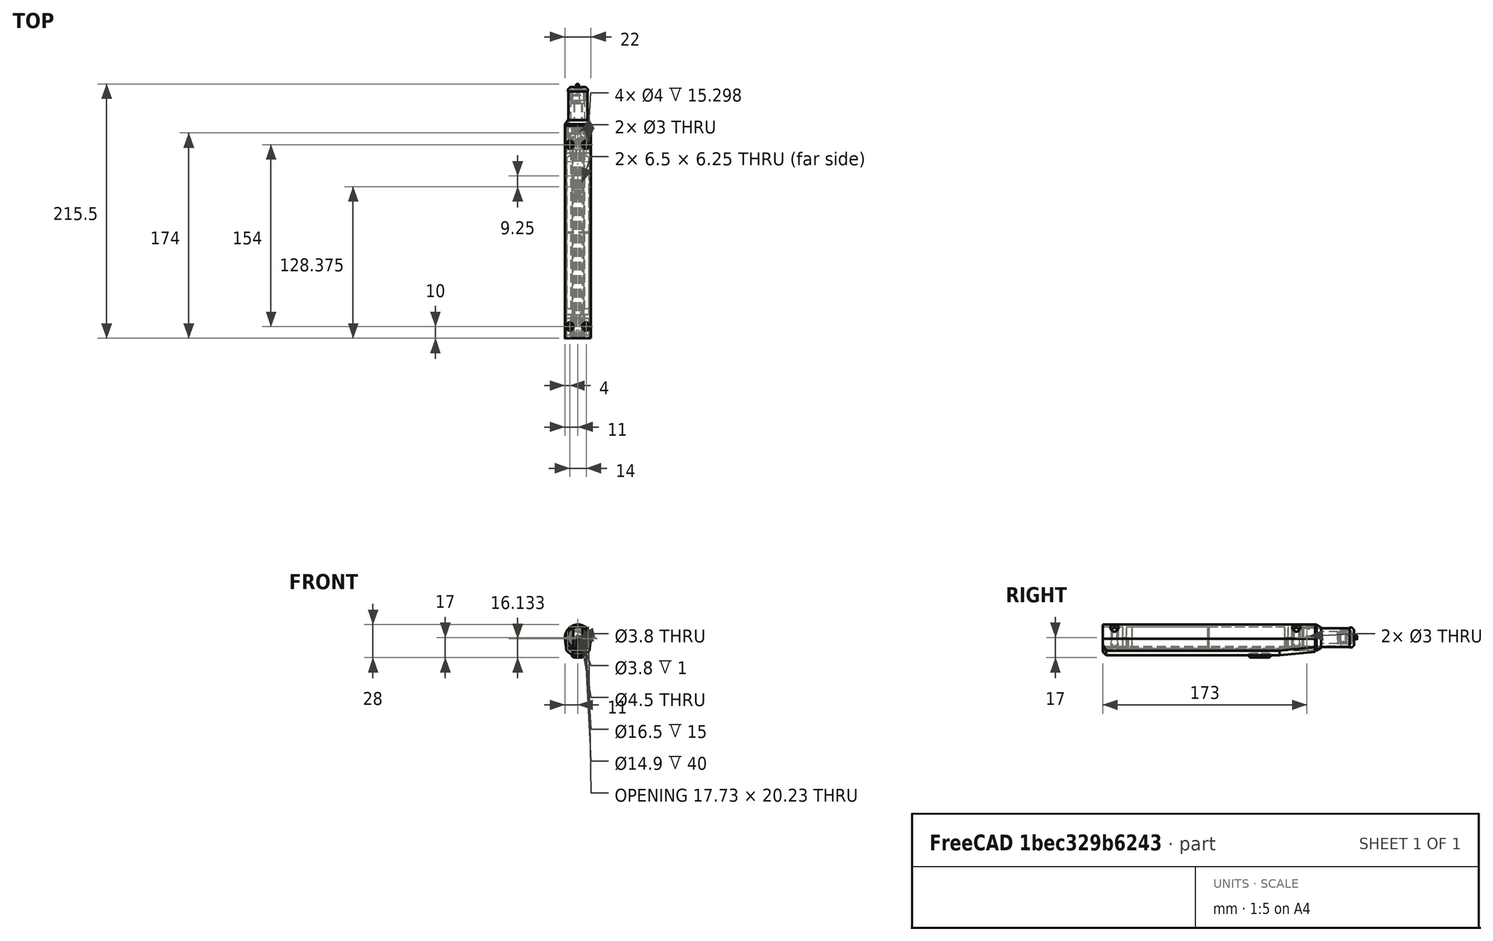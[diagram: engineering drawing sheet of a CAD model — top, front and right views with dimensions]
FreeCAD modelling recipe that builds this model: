
FCSTD DOCUMENT  (FreeCAD 0.20R29177 (Git))
Label: ScrewDriverV5
License: All rights reserved
LicenseURL: http://en.wikipedia.org/wiki/All_rights_reserved
objects: Sketcher::SketchObject×36, PartDesign::Pad×22, PartDesign::Pocket×12, PartDesign::Chamfer×10, PartDesign::Body×8, PartDesign::Fillet×7, PartDesign::Hole×1, PartDesign::Plane×1, PartDesign::LinearPattern×1
note: 150 computed .brp shape members not serialized (recipe doc carries the construction recipe); baked Part::Feature solids carry a one-line shape summary decoded from their .brp

FEATURE [Sketcher::SketchObject] Sketch001
  AttachmentOffset = pos=(0,0,30) rot=(0,0,1;0rad)
  FullyConstrained = true
  MapMode = 5
  Placement = pos=(0,-30,-6.7e-15) rot=(1,0,0;1.5708rad)
  Support = -> [XZ_Plane001]
  sketch-geometry (1):
    g0: Circle CenterX=0 CenterY=15 CenterZ=0 NormalX=0 NormalY=0 NormalZ=1 AngleXU=0 Radius=9
  constraints (3):
    c: PointOnObject(g0,g-2)
    c: Diameter(g0) = 18
    c: DistanceY(g-1,g0) = 15
FEATURE [PartDesign::Pad] Pad001  label="SingleBattery"
  Direction = (0,-1,2e-16)
  Length = 65
  Length2 = 10
  Placement = pos=(0,0,0) rot=(1,0,0;1.5708rad)
  Profile = -> Sketch001
  ReferenceAxis = -> Sketch001 [N_Axis]
  Type = 0
FEATURE [PartDesign::Fillet] Fillet001  label="BatteryFillet"
  Base = -> Pad001 [Edge2,Edge3]
  BaseFeature = -> Pad001
  Placement = pos=(0,0,0) rot=(1,0,0;1.5708rad)
  Radius = 1
  SupportTransform = false
  UseAllEdges = false
FEATURE [PartDesign::Body] Body001  label="18650I"
  Group = -> [Sketch001,Pad001,Fillet001]
  Origin = -> Origin001
  Placement = pos=(0,4,0) rot=(0,0,1;0rad)
  Tip = -> Fillet001
FEATURE [Sketcher::SketchObject] Sketch002
  AttachmentOffset = pos=(0,0,95) rot=(0,0,1;0rad)
  FullyConstrained = true
  MapMode = 5
  Placement = pos=(0,-95,-2.11e-14) rot=(1,0,0;1.5708rad)
  Support = -> [XZ_Plane002]
  sketch-geometry (1):
    g0: Circle CenterX=0 CenterY=15 CenterZ=0 NormalX=0 NormalY=0 NormalZ=1 AngleXU=0 Radius=9
  constraints (3):
    c: PointOnObject(g0,g-2)
    c: Diameter(g0) = 18
    c: DistanceY(g-1,g0) = 15
FEATURE [PartDesign::Pad] Pad002  label="SingleBattery001"
  Direction = (0,-1,-2e-16)
  Length = 65
  Length2 = 10
  Placement = pos=(0,0,0) rot=(1,0,0;1.5708rad)
  Profile = -> Sketch002
  ReferenceAxis = -> Sketch002 [N_Axis]
  Type = 0
FEATURE [PartDesign::Fillet] Fillet002  label="BatteryFillet001"
  Base = -> Pad002 [Edge2,Edge3]
  BaseFeature = -> Pad002
  Placement = pos=(0,0,0) rot=(1,0,0;1.5708rad)
  Radius = 1
  SupportTransform = false
  UseAllEdges = false
FEATURE [PartDesign::Body] Body002  label="18650II"
  Group = -> [Sketch002,Pad002,Fillet002]
  Origin = -> Origin002
  Placement = pos=(0,5,0) rot=(0,0,1;0rad)
  Tip = -> Fillet002
FEATURE [Sketcher::SketchObject] Sketch013
  AttachmentOffset = pos=(0,0,-10) rot=(0,0,1;0rad)
  FullyConstrained = true
  MapMode = 5
  Placement = pos=(0,10,2.2e-15) rot=(1,0,0;1.5708rad)
  Support = -> [XZ_Plane006]
  sketch-geometry (2):
    g0: Circle CenterX=0 CenterY=15 CenterZ=0 NormalX=0 NormalY=0 NormalZ=1 AngleXU=0 Radius=8.25
    g1: Circle CenterX=0 CenterY=15 CenterZ=0 NormalX=0 NormalY=0 NormalZ=1 AngleXU=0 Radius=11
  constraints (5):
    c: PointOnObject(g0,g-2)
    c: DistanceY(g-1,g0) = 15
    c: Diameter(g0) = 16.5
    c: Coincident(g1,g0)
    c: Diameter(g1) = 22
FEATURE [PartDesign::Pad] Pad007
  Direction = (0,-1,-2e-16)
  Length = 15
  Length2 = 10
  Placement = pos=(0,0,0) rot=(1,0,0;1.5708rad)
  Profile = -> Sketch013
  ReferenceAxis = -> Sketch013 [N_Axis]
  Type = 0
FEATURE [Sketcher::SketchObject] Sketch014
  AttachmentOffset = pos=(0,0,7) rot=(0,0,1;0rad)
  FullyConstrained = false
  MapMode = 5
  Placement = pos=(0,-7,-1.6e-15) rot=(1,0,0;1.5708rad)
  Support = -> [XZ_Plane006]
  sketch-geometry (2):
    g0: Circle CenterX=0.134772 CenterY=15 CenterZ=0 NormalX=0 NormalY=0 NormalZ=1 AngleXU=0 Radius=9.25
    g1: Circle CenterX=0.134772 CenterY=15 CenterZ=0 NormalX=0 NormalY=0 NormalZ=1 AngleXU=0 Radius=11.25
  constraints (4):
    c: Diameter(g0) = 18.5
    c: Coincident(g1,g0)
    c: Diameter(g1) = 22.5
    c: DistanceY(g-1,g0) = 15
FEATURE [PartDesign::Pocket] Pocket006
  BaseFeature = -> Pad007
  Direction = (0,1,2e-16)
  Length = 12
  Length2 = 1
  Placement = pos=(0,0,0) rot=(1,0,0;1.5708rad)
  Profile = -> Sketch014
  ReferenceAxis = -> Sketch014 [N_Axis]
  Type = 0
FEATURE [PartDesign::Chamfer] Chamfer006
  Angle = 45
  Base = -> Pocket006 [Edge1]
  BaseFeature = -> Pocket006
  ChamferType = 1
  FlipDirection = false
  Placement = pos=(0,0,0) rot=(1,0,0;1.5708rad)
  Size = 4
  Size2 = 1.5
  SupportTransform = false
  UseAllEdges = false
FEATURE [Sketcher::SketchObject] Sketch015
  AttachmentOffset = pos=(0,4,5) rot=(0,0,1;0rad)
  FullyConstrained = false
  MapMode = 5
  Placement = pos=(0,4,5) rot=(0,0,1;0rad)
  Support = -> [XY_Plane006]
  sketch-geometry (1):
    g0: Circle CenterX=0.028156 CenterY=-7.03327 CenterZ=0 NormalX=0 NormalY=0 NormalZ=1 AngleXU=0 Radius=1.5
  constraints (1):
    c: Diameter(g0) = 3
FEATURE [PartDesign::Hole] Hole
  BaseFeature = -> Chamfer006
  CustomThreadClearance = 0
  Depth = 25
  DepthType = 0
  Diameter = 2.5
  DrillForDepth = false
  DrillPoint = 1
  DrillPointAngle = 118
  HoleCutCountersinkAngle = 90
  HoleCutCustomValues = false
  HoleCutDepth = 0
  HoleCutDiameter = 6.1
  HoleCutType = 0
  ModelThread = false
  Placement = pos=(0,0,0) rot=(1,0,0;1.5708rad)
  Profile = -> Sketch015
  Tapered = false
  TaperedAngle = 90
  ThreadClass = 0
  ThreadDepth = 25
  ThreadDepthType = 0
  ThreadDirection = 0
  ThreadFit = 0
  ThreadSize = 9
  ThreadType = 1
  Threaded = true
  UseCustomThreadClearance = false
FEATURE [PartDesign::Plane] DatumPlane
  Length = 61.4018
  Placement = pos=(0,0,15) rot=(0,0,1;0rad)
  ResizeMode = 0
  Width = 76.4018
FEATURE [Sketcher::SketchObject] Sketch003
  FullyConstrained = true
  MapMode = 5
  Placement = pos=(0,0,0) rot=(1,0,0;1.5708rad)
  Support = -> [XZ_Plane003]
  sketch-geometry (1):
    g0: Circle CenterX=0 CenterY=15 CenterZ=0 NormalX=0 NormalY=0 NormalZ=1 AngleXU=0 Radius=8
  constraints (3):
    c: PointOnObject(g0,g-2)
    c: Diameter(g0) = 16
    c: DistanceY(g-1,g0) = 15
FEATURE [PartDesign::Pad] Pad003
  Direction = (0,-1,-2e-16)
  Length = 40
  Length2 = 10
  Placement = pos=(0,0,0) rot=(1,0,0;1.5708rad)
  Profile = -> Sketch003
  ReferenceAxis = -> Sketch003 [N_Axis]
  Reversed = true
  Type = 0
FEATURE [Sketcher::SketchObject] Sketch004
  FullyConstrained = true
  MapMode = 5
  Placement = pos=(0,0,15) rot=(0,0,1;0rad)
  Support = -> [DatumPlane]
  sketch-geometry (1):
    g0: Circle CenterX=0 CenterY=5 CenterZ=0 NormalX=0 NormalY=0 NormalZ=1 AngleXU=0 Radius=1.5
  constraints (3):
    c: PointOnObject(g0,g-2)
    c: Diameter(g0) = 3
    c: DistanceY(g-1,g0) = 5
FEATURE [PartDesign::Pocket] Pocket
  BaseFeature = -> Pad003
  Direction = (0,0,-1)
  Length = 27
  Length2 = 5
  Midplane = true
  Placement = pos=(0,0,0) rot=(1,0,0;1.5708rad)
  Profile = -> Sketch004
  ReferenceAxis = -> Sketch004 [N_Axis]
  Type = 0
FEATURE [Sketcher::SketchObject] Sketch005
  ExternalGeometry = -> [Pocket]
  FullyConstrained = true
  MapMode = 5
  Placement = pos=(0,0,0) rot=(1,0,0;1.5708rad)
  Support = -> [XZ_Plane003]
  sketch-geometry (1):
    g0: Circle CenterX=0 CenterY=15 CenterZ=0 NormalX=0 NormalY=0 NormalZ=1 AngleXU=0 Radius=7.45
  constraints (3):
    c: Coincident(g0,g-3)
    c: Diameter(g-3) = 16
    c: Diameter(g0) = 14.9
FEATURE [PartDesign::Pocket] Pocket001
  BaseFeature = -> Pocket
  Direction = (0,1,2e-16)
  Length = 5
  Length2 = 5
  Placement = pos=(0,0,0) rot=(1,0,0;1.5708rad)
  Profile = -> Sketch005
  ReferenceAxis = -> Sketch005 [N_Axis]
  Type = 1
FEATURE [Sketcher::SketchObject] Sketch016
  FullyConstrained = false
  MapMode = 5
  Support = -> [XY_Plane003]
  sketch-geometry (1):
    g0: Circle CenterX=0 CenterY=4.973 CenterZ=0 NormalX=0 NormalY=0 NormalZ=1 AngleXU=0 Radius=1.25
  constraints (2):
    c: PointOnObject(g0,g-2)
    c: Diameter(g0) = 2.5
FEATURE [PartDesign::Body] Body003  label="MetalPipe"
  Group = -> [Sketch003,Pad003,DatumPlane,Sketch004,Pocket,Sketch005,Pocket001,Sketch016]
  Origin = -> Origin003
  Placement = pos=(0,-11,0) rot=(0,0,1;0rad)
  Tip = -> Pocket001
FEATURE [PartDesign::Chamfer] Chamfer008
  Angle = 45
  Base = -> Hole [Edge5]
  BaseFeature = -> Hole
  ChamferType = 1
  FlipDirection = false
  Placement = pos=(0,0,0) rot=(1,0,0;1.5708rad)
  Size = 4
  Size2 = 1
  SupportTransform = false
  UseAllEdges = false
FEATURE [Sketcher::SketchObject] Sketch022
  FullyConstrained = true
  MapMode = 5
  Placement = pos=(0,0,0) rot=(1,0,0;1.5708rad)
  Support = -> [XZ_Plane007]
  sketch-geometry (4):
    g0: LineSegment StartX=-3.5 StartY=19.8734 StartZ=0 EndX=3.5 EndY=19.8734 EndZ=0
    g1: LineSegment StartX=3.11736 StartY=9.8734 StartZ=0 EndX=-3.11736 EndY=9.8734 EndZ=0
    g2: ArcOfCircle CenterX=0 CenterY=15 CenterZ=0 NormalX=0 NormalY=0 NormalZ=1 AngleXU=0 Radius=6 StartAngle=2.19362 EndAngle=4.16605
    g3: ArcOfCircle CenterX=0 CenterY=15 CenterZ=0 NormalX=0 NormalY=0 NormalZ=1 AngleXU=0 Radius=6 StartAngle=5.25873 EndAngle=7.23116
  constraints (13):
    c: Horizontal(g0)
    c: Horizontal(g1)
    c: PointOnObject(g2,g-2)
    c: DistanceY(g-1,g2) = 15
    c: Coincident(g3,g0)
    c: Coincident(g2,g0)
    c: Equal(g2,g3)
    c: Coincident(g2,g1)
    c: Coincident(g2,g3)
    c: DistanceX(g0,g0) = 7
    c: DistanceY(g1,g0) = 10
    c: Coincident(g3,g1)
    c: Radius(g2) = 6
FEATURE [PartDesign::Pad] Pad011
  Direction = (0,-1,2e-16)
  Length = 14.6
  Length2 = 10
  Placement = pos=(0,0,0) rot=(1,0,0;1.5708rad)
  Profile = -> Sketch022
  ReferenceAxis = -> Sketch022 [N_Axis]
  Type = 0
FEATURE [Sketcher::SketchObject] Sketch023
  ExternalGeometry = -> [Pad011]
  FullyConstrained = true
  MapMode = 5
  Placement = pos=(0,0,0) rot=(-1,0,0;1.5708rad)
  Support = -> [Pad011]
  sketch-geometry (4):
    g0: LineSegment StartX=-6 StartY=-10 StartZ=0 EndX=6 EndY=-10 EndZ=0
    g1: LineSegment StartX=6 StartY=-10 StartZ=0 EndX=6 EndY=-20 EndZ=0
    g2: LineSegment StartX=6 StartY=-20 StartZ=0 EndX=-6 EndY=-20 EndZ=0
    g3: LineSegment StartX=-6 StartY=-20 StartZ=0 EndX=-6 EndY=-10 EndZ=0
  constraints (12):
    c: Coincident(g0,g1)
    c: Coincident(g1,g2)
    c: Coincident(g2,g3)
    c: Coincident(g3,g0)
    c: Horizontal(g0)
    c: Horizontal(g2)
    c: Vertical(g1)
    c: Vertical(g3)
    c: DistanceX(g0,g0) = 12
    c: DistanceX(g-3,g0) = 6
    c: DistanceY(g-3,g0) = 5
    c: DistanceY(g1,g-3) = 5
FEATURE [PartDesign::Pad] Pad012
  BaseFeature = -> Pad011
  Direction = (0,1,-2e-16)
  Length = 1
  Length2 = 10
  Placement = pos=(0,0,0) rot=(1,0,0;1.5708rad)
  Profile = -> Sketch023
  ReferenceAxis = -> Sketch023 [N_Axis]
  Type = 0
FEATURE [PartDesign::Fillet] Fillet003
  Base = -> Pad012 [Edge28,Edge26,Edge25,Edge30]
  BaseFeature = -> Pad012
  Placement = pos=(0,0,0) rot=(1,0,0;1.5708rad)
  Radius = 0.5
  SupportTransform = false
  UseAllEdges = false
FEATURE [Sketcher::SketchObject] Sketch024
  FullyConstrained = false
  MapMode = 5
  Placement = pos=(0,0,0) rot=(1,0,0;1.5708rad)
  Support = -> [XZ_Plane007]
  sketch-geometry (4):
    g0: Circle CenterX=-5.3769 CenterY=19.2954 CenterZ=0 NormalX=0 NormalY=0 NormalZ=1 AngleXU=0 Radius=0.455689
    g1: Circle CenterX=-5.39544 CenterY=10.6161 CenterZ=0 NormalX=0 NormalY=0 NormalZ=1 AngleXU=0 Radius=0.455689
    g2: Circle CenterX=5.39544 CenterY=10.6161 CenterZ=0 NormalX=0 NormalY=0 NormalZ=1 AngleXU=0 Radius=0.455689
    g3: Circle CenterX=5.3769 CenterY=19.2954 CenterZ=0 NormalX=0 NormalY=0 NormalZ=1 AngleXU=0 Radius=0.455689
  constraints (5):
    c: Equal(g3,g2)
    c: Equal(g2,g1)
    c: Equal(g1,g0)
    c: Symmetric(g3,g0,g-2)
    c: Symmetric(g2,g1,g-2)
FEATURE [PartDesign::Pad] Pad013
  BaseFeature = -> Fillet003
  Direction = (0,-1,2e-16)
  Length = 7.5
  Length2 = 10
  Placement = pos=(0,0,0) rot=(1,0,0;1.5708rad)
  Profile = -> Sketch024
  ReferenceAxis = -> Sketch024 [N_Axis]
  Reversed = true
  Type = 0
FEATURE [Sketcher::SketchObject] Sketch025
  AttachmentOffset = pos=(0,0,-7.5) rot=(0,0,1;0rad)
  ExternalGeometry = -> [Pad013]
  FullyConstrained = true
  MapMode = 5
  Placement = pos=(0,7.5,1.7e-15) rot=(1,0,0;1.5708rad)
  Support = -> [XZ_Plane007]
  sketch-geometry (4):
    g0: LineSegment StartX=-6 StartY=20 StartZ=0 EndX=6 EndY=20 EndZ=0
    g1: LineSegment StartX=6 StartY=20 StartZ=0 EndX=6 EndY=10 EndZ=0
    g2: LineSegment StartX=6 StartY=10 StartZ=0 EndX=-6 EndY=10 EndZ=0
    g3: LineSegment StartX=-6 StartY=10 StartZ=0 EndX=-6 EndY=20 EndZ=0
  constraints (12):
    c: Coincident(g0,g1)
    c: Coincident(g1,g2)
    c: Coincident(g2,g3)
    c: Coincident(g3,g0)
    c: Horizontal(g0)
    c: Horizontal(g2)
    c: Vertical(g1)
    c: Vertical(g3)
    c: DistanceX(g0,g0) = 12
    c: DistanceX(g0,g-3) = 6
    c: DistanceY(g1,g1) = 10
    c: DistanceY(g-3,g0) = 5
FEATURE [PartDesign::Pad] Pad014
  BaseFeature = -> Pad013
  Direction = (0,-1,2e-16)
  Length = 1
  Length2 = 10
  Placement = pos=(0,0,0) rot=(1,0,0;1.5708rad)
  Profile = -> Sketch025
  ReferenceAxis = -> Sketch025 [N_Axis]
  Type = 0
FEATURE [Sketcher::SketchObject] Sketch026
  ExternalGeometry = -> [Pad014]
  FullyConstrained = true
  MapMode = 5
  Placement = pos=(0,7.5,-3e-15) rot=(-1,0,0;1.5708rad)
  Support = -> [Pad014]
  sketch-geometry (1):
    g0: Circle CenterX=0 CenterY=-15 CenterZ=0 NormalX=0 NormalY=0 NormalZ=1 AngleXU=0 Radius=1.9
  constraints (2):
    c: Coincident(g0,g-3)
    c: Diameter(g0) = 3.8
FEATURE [PartDesign::Pocket] Pocket008
  BaseFeature = -> Pad014
  Direction = (0,-1,2e-16)
  Length = 7.5
  Length2 = 5
  Placement = pos=(0,0,0) rot=(1,0,0;1.5708rad)
  Profile = -> Sketch026
  ReferenceAxis = -> Sketch026 [N_Axis]
  Type = 0
FEATURE [Sketcher::SketchObject] Sketch027
  ExternalGeometry = -> [Pocket008]
  FullyConstrained = true
  MapMode = 5
  Placement = pos=(0,7.5,-3e-15) rot=(-1,0,0;1.5708rad)
  Support = -> [Pocket008]
  sketch-geometry (1):
    g0: Circle CenterX=0 CenterY=-15 CenterZ=0 NormalX=0 NormalY=0 NormalZ=1 AngleXU=0 Radius=1.45
  constraints (2):
    c: Coincident(g0,g-3)
    c: Diameter(g0) = 2.9
FEATURE [PartDesign::Pad] Pad015
  BaseFeature = -> Pocket008
  Direction = (0,1,-2e-16)
  Length = 18
  Length2 = 10
  Midplane = true
  Placement = pos=(0,0,0) rot=(1,0,0;1.5708rad)
  Profile = -> Sketch027
  ReferenceAxis = -> Sketch027 [N_Axis]
  Type = 0
FEATURE [PartDesign::Fillet] Fillet004
  Base = -> Pad015 [Edge70,Edge73,Edge75,Edge71]
  BaseFeature = -> Pad015
  Placement = pos=(0,0,0) rot=(1,0,0;1.5708rad)
  Radius = 0.5
  SupportTransform = false
  UseAllEdges = false
FEATURE [Sketcher::SketchObject] Sketch028
  AttachmentOffset = pos=(0,0,-7) rot=(0,0,1;0rad)
  ExternalGeometry = -> [Fillet004]
  FullyConstrained = true
  MapMode = 5
  Placement = pos=(0,7,1.6e-15) rot=(1,0,0;1.5708rad)
  Support = -> [XZ_Plane007]
  sketch-geometry (2):
    g0: ArcOfCircle CenterX=0 CenterY=15 CenterZ=0 NormalX=0 NormalY=0 NormalZ=1 AngleXU=0 Radius=1.45 StartAngle=5.38201 EndAngle=7.18436
    g1: LineSegment StartX=0.9 StartY=13.8631 StartZ=0 EndX=0.9 EndY=16.1369 EndZ=0
  constraints (6):
    c: Coincident(g0,g-3)
    c: PointOnObject(g0,g-3)
    c: DistanceX(g0,g0) = 0.9
    c: DistanceX(g0,g0) = 0.9
    c: Coincident(g1,g0)
    c: Coincident(g1,g0)
FEATURE [PartDesign::Pocket] Pocket009
  BaseFeature = -> Fillet004
  Direction = (0,1,-2e-16)
  Length = 10
  Length2 = 5
  Placement = pos=(0,0,0) rot=(1,0,0;1.5708rad)
  Profile = -> Sketch028
  ReferenceAxis = -> Sketch028 [N_Axis]
  Type = 0
FEATURE [PartDesign::Body] Body007  label="Engine"
  Group = -> [Sketch022,Pad011,Sketch023,Pad012,Fillet003,Sketch024,Pad013,Sketch025,Pad014,Sketch026,Pocket008,Sketch027,Pad015,Fillet004,Sketch028,Pocket009]
  Origin = -> Origin007
  Placement = pos=(0,19,0) rot=(0,0,1;0rad)
  Tip = -> Pocket009
FEATURE [Sketcher::SketchObject] Sketch029
  FullyConstrained = true
  MapMode = 5
  Placement = pos=(0,0,0) rot=(1,0,0;1.5708rad)
  Support = -> [XZ_Plane008]
  sketch-geometry (2):
    g0: Circle CenterX=0 CenterY=15 CenterZ=0 NormalX=0 NormalY=0 NormalZ=1 AngleXU=0 Radius=2.25
    g1: Circle CenterX=0 CenterY=15 CenterZ=0 NormalX=0 NormalY=0 NormalZ=1 AngleXU=0 Radius=7.35
  constraints (5):
    c: PointOnObject(g0,g-2)
    c: Coincident(g1,g0)
    c: DistanceY(g-1,g0) = 15
    c: Diameter(g0) = 4.5
    c: Diameter(g1) = 14.7
FEATURE [PartDesign::Pad] Pad016
  Direction = (0,-1,2e-16)
  Length = 2.5
  Length2 = 10
  Placement = pos=(0,0,0) rot=(1,0,0;1.5708rad)
  Profile = -> Sketch029
  ReferenceAxis = -> Sketch029 [N_Axis]
  Reversed = true
  Type = 0
FEATURE [Sketcher::SketchObject] Sketch030
  ExternalGeometry = -> [Pad016]
  FullyConstrained = false
  MapMode = 5
  Placement = pos=(0,2.5,-1.1e-15) rot=(-1,0,0;1.5708rad)
  Support = -> [Pad016]
  sketch-geometry (8):
    g0: LineSegment StartX=-4.88664 StartY=-20.4903 StartZ=0 EndX=4.88664 EndY=-20.4903 EndZ=0
    g1: LineSegment StartX=6.43814 StartY=-18.5458 StartZ=0 EndX=6.43814 EndY=-11.4542 EndZ=0
    g2: LineSegment StartX=4.68852 StartY=-9.33959 StartZ=0 EndX=-4.68852 EndY=-9.33959 EndZ=0
    g3: LineSegment StartX=-6.45711 StartY=-11.4888 StartZ=0 EndX=-6.45711 EndY=-18.5112 EndZ=0
    g4: ArcOfCircle CenterX=0 CenterY=-15 CenterZ=0 NormalX=0 NormalY=0 NormalZ=1 AngleXU=0 Radius=7.35 StartAngle=2.64355 EndAngle=3.63964
    g5: ArcOfCircle CenterX=0 CenterY=-15 CenterZ=0 NormalX=0 NormalY=0 NormalZ=1 AngleXU=0 Radius=7.35 StartAngle=3.9851 EndAngle=5.43968
    g6: ArcOfCircle CenterX=0 CenterY=-15 CenterZ=0 NormalX=0 NormalY=0 NormalZ=1 AngleXU=0 Radius=7.35 StartAngle=5.77977 EndAngle=6.7866
    g7: ArcOfCircle CenterX=0 CenterY=-15 CenterZ=0 NormalX=0 NormalY=0 NormalZ=1 AngleXU=0 Radius=7.35 StartAngle=0.879035 EndAngle=2.26256
  constraints (26):
    c: PointOnObject(g0,g-3)
    c: PointOnObject(g0,g-3)
    c: Horizontal(g0)
    c: PointOnObject(g1,g-3)
    c: PointOnObject(g1,g-3)
    c: Vertical(g1)
    c: PointOnObject(g2,g-3)
    c: PointOnObject(g2,g-3)
    c: Horizontal(g2)
    c: PointOnObject(g3,g-3)
    c: Vertical(g3)
    c: Coincident(g4,g-3)
    c: Coincident(g7,g2)
    c: Coincident(g4,g3)
    c: Equal(g4,g5)
    c: PointOnObject(g4,g3)
    c: PointOnObject(g5,g0)
    c: Coincident(g4,g5)
    c: Equal(g5,g6)
    c: PointOnObject(g5,g0)
    c: PointOnObject(g6,g1)
    c: Coincident(g5,g6)
    c: Equal(g6,g7)
    c: PointOnObject(g6,g1)
    c: PointOnObject(g7,g2)
    c: Coincident(g6,g7)
FEATURE [PartDesign::Pad] Pad017
  BaseFeature = -> Pad016
  Direction = (0,1,-2e-16)
  Length = 9
  Length2 = 10
  Placement = pos=(0,0,0) rot=(1,0,0;1.5708rad)
  Profile = -> Sketch030
  ReferenceAxis = -> Sketch030 [N_Axis]
  Type = 0
FEATURE [PartDesign::Chamfer] Chamfer010
  Angle = 45
  Base = -> Pad017 [Edge12]
  BaseFeature = -> Pad017
  ChamferType = 1
  FlipDirection = false
  Placement = pos=(0,0,0) rot=(1,0,0;1.5708rad)
  Size = 2
  Size2 = 2
  SupportTransform = false
  UseAllEdges = false
FEATURE [Sketcher::SketchObject] Sketch031
  ExternalGeometry = -> [Chamfer010]
  FullyConstrained = true
  MapMode = 5
  Placement = pos=(0,0,0) rot=(1,0,0;1.5708rad)
  Support = -> [Chamfer010]
  sketch-geometry (2):
    g0: Circle CenterX=0 CenterY=15 CenterZ=0 NormalX=0 NormalY=0 NormalZ=1 AngleXU=0 Radius=8.4
    g1: Circle CenterX=0 CenterY=15 CenterZ=0 NormalX=0 NormalY=0 NormalZ=1 AngleXU=0 Radius=7.35
  constraints (4):
    c: Coincident(g0,g-3)
    c: Diameter(g0) = 16.8
    c: Coincident(g1,g0)
    c: Diameter(g1) = 14.7
FEATURE [PartDesign::Pad] Pad018
  BaseFeature = -> Chamfer010
  Direction = (0,-1,4e-16)
  Length = 4
  Length2 = 10
  Placement = pos=(0,0,0) rot=(1,0,0;1.5708rad)
  Profile = -> Sketch031
  ReferenceAxis = -> Sketch031 [N_Axis]
  Reversed = true
  Type = 0
FEATURE [PartDesign::Chamfer] Chamfer011
  Angle = 45
  Base = -> Pad018 [Edge5]
  BaseFeature = -> Pad018
  ChamferType = 0
  FlipDirection = false
  Placement = pos=(0,0,0) rot=(1,0,0;1.5708rad)
  Size = 2
  Size2 = 1
  SupportTransform = false
  UseAllEdges = false
FEATURE [PartDesign::Fillet] Fillet005
  Base = -> Chamfer011 [Edge4]
  BaseFeature = -> Chamfer011
  Placement = pos=(0,0,0) rot=(1,0,0;1.5708rad)
  Radius = 1
  SupportTransform = false
  UseAllEdges = false
FEATURE [PartDesign::Body] Body008  label="EngineHolder"
  Group = -> [Sketch029,Pad016,Sketch030,Pad017,Chamfer010,Sketch031,Pad018,Chamfer011,Fillet005]
  Origin = -> Origin008
  Placement = pos=(0,33,30) rot=(1,0,0;3.14159rad)
  Tip = -> Fillet005
FEATURE [Sketcher::SketchObject] Sketch035
  FullyConstrained = true
  MapMode = 5
  Support = -> [XY_Plane009]
  sketch-geometry (4):
    g0: LineSegment StartX=-5.5 StartY=-37 StartZ=0 EndX=5.5 EndY=-37 EndZ=0
    g1: LineSegment StartX=5.5 StartY=-37 StartZ=0 EndX=5.5 EndY=-57 EndZ=0
    g2: LineSegment StartX=5.5 StartY=-57 StartZ=0 EndX=-5.5 EndY=-57 EndZ=0
    g3: LineSegment StartX=-5.5 StartY=-57 StartZ=0 EndX=-5.5 EndY=-37 EndZ=0
  constraints (12):
    c: Coincident(g0,g1)
    c: Coincident(g1,g2)
    c: Coincident(g2,g3)
    c: Coincident(g3,g0)
    c: Horizontal(g0)
    c: Horizontal(g2)
    c: Vertical(g1)
    c: Vertical(g3)
    c: DistanceY(g0,g-1) = 37
    c: DistanceX(g0,g-1) = 5.5
    c: DistanceX(g-1,g1) = 5.5
    c: DistanceY(g1,g1) = 20
FEATURE [PartDesign::Pad] Pad019
  Direction = (0,0,1)
  Length = 2
  Length2 = 10
  Profile = -> Sketch035
  ReferenceAxis = -> Sketch035 [N_Axis]
  Reversed = true
  Type = 0
FEATURE [Sketcher::SketchObject] Sketch036
  ExternalGeometry = -> [Pad019]
  FullyConstrained = true
  MapMode = 5
  Support = -> [XY_Plane009]
  sketch-geometry (8):
    g0: LineSegment StartX=-3.25 StartY=-39.25 StartZ=0 EndX=3.25 EndY=-39.25 EndZ=0
    g1: LineSegment StartX=3.25 StartY=-39.25 StartZ=0 EndX=3.25 EndY=-45.5 EndZ=0
    g2: LineSegment StartX=3.25 StartY=-54.75 StartZ=0 EndX=-3.25 EndY=-54.75 EndZ=0
    g3: LineSegment StartX=-3.25 StartY=-54.75 StartZ=0 EndX=-3.25 EndY=-48.5 EndZ=0
    g4: LineSegment StartX=-3.25 StartY=-45.5 StartZ=0 EndX=3.25 EndY=-45.5 EndZ=0
    g5: LineSegment StartX=3.25 StartY=-48.5 StartZ=0 EndX=-3.25 EndY=-48.5 EndZ=0
    g6: LineSegment StartX=3.25 StartY=-48.5 StartZ=0 EndX=3.25 EndY=-54.75 EndZ=0
    g7: LineSegment StartX=-3.25 StartY=-45.5 StartZ=0 EndX=-3.25 EndY=-39.25 EndZ=0
  constraints (24):
    c: Coincident(g0,g1)
    c: Coincident(g6,g2)
    c: Coincident(g2,g3)
    c: Coincident(g7,g0)
    c: Horizontal(g0)
    c: Horizontal(g2)
    c: Vertical(g1)
    c: Vertical(g3)
    c: DistanceX(g-5,g0) = 2.25
    c: Horizontal(g4)
    c: Horizontal(g5)
    c: DistanceY(g4,g0) = 6.25
    c: DistanceY(g6,g5) = 6.25
    c: Coincident(g7,g4)
    c: Vertical(g6)
    c: Coincident(g6,g5)
    c: DistanceX(g0,g0) = 6.5
    c: DistanceX(g5,g5) = 6.5
    c: Coincident(g5,g3)
    c: Coincident(g4,g1)
    c: Vertical(g7)
    c: DistanceY(g-5,g2) = 2.25
    c: DistanceX(g-5,g2) = 2.25
    c: DistanceY(g0,g-4) = 2.25
FEATURE [PartDesign::Pocket] Pocket012
  BaseFeature = -> Pad019
  Direction = (0,0,-1)
  Length = 5
  Length2 = 5
  Profile = -> Sketch036
  ReferenceAxis = -> Sketch036 [N_Axis]
  Type = 0
FEATURE [PartDesign::Fillet] Fillet007
  Base = -> Pocket012 [Edge1,Edge2,Edge8,Edge5]
  BaseFeature = -> Pocket012
  Radius = 2
  SupportTransform = false
  UseAllEdges = false
FEATURE [PartDesign::Chamfer] Chamfer
  Angle = 45
  Base = -> Fillet007 [Edge4,Edge21,Edge23,Edge25,Edge27,Edge28,Edge24,Edge26]
  BaseFeature = -> Fillet007
  ChamferType = 0
  FlipDirection = false
  Size = 1.9
  Size2 = 1
  SupportTransform = false
  UseAllEdges = false
FEATURE [Sketcher::SketchObject] Sketch037
  AttachmentOffset = pos=(0,0,36) rot=(0,0,1;0rad)
  ExternalGeometry = -> [Sketch035]
  FullyConstrained = false
  MapMode = 5
  Placement = pos=(0,-36,-8e-15) rot=(1,0,0;1.5708rad)
  Support = -> [XZ_Plane009]
  sketch-geometry (8):
    g0: LineSegment StartX=4.99997 StartY=0 StartZ=0 EndX=6.38463 EndY=0 EndZ=0
    g1: LineSegment StartX=6.38463 StartY=0 StartZ=0 EndX=6.38463 EndY=-1.93807 EndZ=0
    g2: LineSegment StartX=6.38463 StartY=-1.93807 StartZ=0 EndX=4.99997 EndY=-1.93807 EndZ=0
    g3: LineSegment StartX=4.99997 StartY=-1.93807 StartZ=0 EndX=4.99997 EndY=0 EndZ=0
    g4: LineSegment StartX=-5.00036 StartY=0 StartZ=0 EndX=-5.88621 EndY=0 EndZ=0
    g5: LineSegment StartX=-5.88621 StartY=0 StartZ=0 EndX=-5.88621 EndY=-2.0574 EndZ=0
    g6: LineSegment StartX=-5.88621 StartY=-2.0574 StartZ=0 EndX=-5.00036 EndY=-2.0574 EndZ=0
    g7: LineSegment StartX=-5.00036 StartY=-2.0574 StartZ=0 EndX=-5.00036 EndY=0 EndZ=0
  constraints (18):
    c: Coincident(g0,g1)
    c: Coincident(g1,g2)
    c: Coincident(g2,g3)
    c: Coincident(g3,g0)
    c: Horizontal(g0)
    c: Horizontal(g2)
    c: Vertical(g1)
    c: Vertical(g3)
    c: PointOnObject(g0,g-1)
    c: Coincident(g4,g5)
    c: Coincident(g5,g6)
    c: Coincident(g6,g7)
    c: Coincident(g7,g4)
    c: Horizontal(g4)
    c: Horizontal(g6)
    c: Vertical(g5)
    c: Vertical(g7)
    c: PointOnObject(g4,g-1)
FEATURE [PartDesign::Pocket] Pocket013
  BaseFeature = -> Chamfer
  Direction = (0,1,2e-16)
  Length = 22
  Length2 = 5
  Profile = -> Sketch037
  ReferenceAxis = -> Sketch037 [N_Axis]
  Reversed = true
  Type = 0
FEATURE [PartDesign::Fillet] Fillet008
  Base = -> Pocket013 [Edge51,Edge32,Edge31,Edge50,Edge29,Edge48]
  BaseFeature = -> Pocket013
  Radius = 0.5
  SupportTransform = false
  UseAllEdges = false
FEATURE [Sketcher::SketchObject] Sketch045
  ExternalGeometry = -> [Fillet008]
  FullyConstrained = true
  MapMode = 5
  Support = -> [XY_Plane009]
  sketch-geometry (12):
    g0: LineSegment StartX=-3.25 StartY=-39.25 StartZ=0 EndX=3.25 EndY=-39.25 EndZ=0
    g1: LineSegment StartX=3.25 StartY=-39.25 StartZ=0 EndX=3.25 EndY=-45.5 EndZ=0
    g2: LineSegment StartX=3.25 StartY=-45.5 StartZ=0 EndX=-3.25 EndY=-45.5 EndZ=0
    g3: LineSegment StartX=-3.25 StartY=-45.5 StartZ=0 EndX=-3.25 EndY=-39.25 EndZ=0
    g4: LineSegment StartX=-3.25 StartY=-48.5 StartZ=0 EndX=3.25 EndY=-48.5 EndZ=0
    g5: LineSegment StartX=3.25 StartY=-48.5 StartZ=0 EndX=3.25 EndY=-54.75 EndZ=0
    g6: LineSegment StartX=3.25 StartY=-54.75 StartZ=0 EndX=-3.25 EndY=-54.75 EndZ=0
    g7: LineSegment StartX=-3.25 StartY=-54.75 StartZ=0 EndX=-3.25 EndY=-48.5 EndZ=0
    g8: LineSegment StartX=-4.5 StartY=-38 StartZ=0 EndX=4.5 EndY=-38 EndZ=0
    g9: LineSegment StartX=4.5 StartY=-38 StartZ=0 EndX=4.5 EndY=-56 EndZ=0
    g10: LineSegment StartX=4.5 StartY=-56 StartZ=0 EndX=-4.5 EndY=-56 EndZ=0
    g11: LineSegment StartX=-4.5 StartY=-56 StartZ=0 EndX=-4.5 EndY=-38 EndZ=0
  constraints (32):
    c: Coincident(g0,g1)
    c: Coincident(g1,g2)
    c: Coincident(g2,g3)
    c: Coincident(g3,g0)
    c: Horizontal(g0)
    c: Horizontal(g2)
    c: Vertical(g1)
    c: Vertical(g3)
    c: Coincident(g0,g-10)
    c: Coincident(g1,g-8)
    c: Coincident(g4,g5)
    c: Coincident(g5,g6)
    c: Coincident(g6,g7)
    c: Coincident(g7,g4)
    c: Horizontal(g4)
    c: Horizontal(g6)
    c: Vertical(g5)
    c: Vertical(g7)
    c: Coincident(g4,g-4)
    c: Coincident(g5,g-6)
    c: Coincident(g8,g9)
    c: Coincident(g9,g10)
    c: Coincident(g10,g11)
    c: Coincident(g11,g8)
    c: Horizontal(g8)
    c: Horizontal(g10)
    c: Vertical(g9)
    c: Vertical(g11)
    c: DistanceX(g8,g-1) = 4.5
    c: DistanceX(g-1,g8) = 4.5
    c: DistanceY(g9,g9) = 18
    c: DistanceY(g8,g-1) = 38
FEATURE [PartDesign::Pad] Pad021
  BaseFeature = -> Fillet008
  Direction = (0,0,1)
  Length = 1.5
  Length2 = 10
  Profile = -> Sketch045
  ReferenceAxis = -> Sketch045 [N_Axis]
  Type = 0
FEATURE [PartDesign::Body] Body009  label="ButtonFrame"
  Group = -> [Sketch035,Pad019,Sketch036,Pocket012,Fillet007,Chamfer,Sketch037,Pocket013,Fillet008,Sketch045,Pad021]
  Origin = -> Origin009
  Tip = -> Pad021
FEATURE [Sketcher::SketchObject] Sketch054
  AttachmentOffset = pos=(0,0,10) rot=(0,0,1;0rad)
  ExternalGeometry = -> [Chamfer008]
  FullyConstrained = true
  MapMode = 5
  Placement = pos=(10,-2.2e-15,2.2e-15) rot=(0.57735,0.57735,0.57735;2.0944rad)
  Support = -> [YZ_Plane006]
  sketch-geometry (1):
    g0: Circle CenterX=-2 CenterY=15 CenterZ=0 NormalX=0 NormalY=0 NormalZ=1 AngleXU=0 Radius=1.5
  constraints (3):
    c: PointOnObject(g0,g-3)
    c: Diameter(g0) = 3
    c: DistanceX(g-3,g0) = 3
FEATURE [PartDesign::Pocket] Pocket021
  BaseFeature = -> Chamfer008
  Direction = (-1,2e-16,-3e-16)
  Length = 20
  Length2 = 5
  Placement = pos=(0,0,0) rot=(1,0,0;1.5708rad)
  Profile = -> Sketch054
  ReferenceAxis = -> Sketch054 [N_Axis]
  Type = 0
FEATURE [PartDesign::Body] Body006  label="HeadLead"
  Group = -> [Sketch013,Pad007,Sketch014,Pocket006,Chamfer006,Sketch015,Hole,Chamfer008,Sketch054,Pocket021]
  Origin = -> Origin006
  Placement = pos=(0,-5,0) rot=(0,0,1;0rad)
  Tip = -> Pocket021
FEATURE [Sketcher::SketchObject] Sketch055
  FullyConstrained = true
  MapMode = 5
  Placement = pos=(0,0,0) rot=(1,0,0;1.5708rad)
  Support = -> [XZ_Plane011]
  sketch-geometry (16):
    g0: ArcOfCircle CenterX=0 CenterY=15 CenterZ=0 NormalX=0 NormalY=0 NormalZ=1 AngleXU=0 Radius=9.25 StartAngle=4.25135 EndAngle=4.49458
    g1: ArcOfCircle CenterX=0 CenterY=15 CenterZ=0 NormalX=0 NormalY=0 NormalZ=1 AngleXU=0 Radius=11 StartAngle=2.38514 EndAngle=3.23263
    g2: LineSegment StartX=-10.9545 StartY=14 StartZ=0 EndX=-9 EndY=0 EndZ=0
    g3: LineSegment StartX=10.9545 StartY=14 StartZ=0 EndX=9 EndY=0 EndZ=0
    g4: LineSegment StartX=9 StartY=0 StartZ=0 EndX=-9 EndY=0 EndZ=0
    g5: LineSegment StartX=-5 StartY=26 StartZ=0 EndX=5 EndY=26 EndZ=0
    g6: LineSegment StartX=-5 StartY=26 StartZ=0 EndX=-8 EndY=22.5498 EndZ=0
    g7: LineSegment StartX=5 StartY=26 StartZ=0 EndX=8 EndY=22.5498 EndZ=0
    g8: ArcOfCircle CenterX=0 CenterY=15 CenterZ=0 NormalX=0 NormalY=0 NormalZ=1 AngleXU=0 Radius=11 StartAngle=6.19215 EndAngle=7.03964
    g9: ArcOfCircle CenterX=-1.75 CenterY=5 CenterZ=0 NormalX=0 NormalY=0 NormalZ=1 AngleXU=0 Radius=1 StartAngle=1.82227 EndAngle=7.25601
    g10: ArcOfCircle CenterX=-5 CenterY=6.25 CenterZ=0 NormalX=0 NormalY=0 NormalZ=1 AngleXU=0 Radius=1 StartAngle=1.6188 EndAngle=6.76769
    g11: ArcOfCircle CenterX=1.75 CenterY=5 CenterZ=0 NormalX=0 NormalY=0 NormalZ=1 AngleXU=0 Radius=1 StartAngle=2.16876 EndAngle=7.6025
    g12: ArcOfCircle CenterX=5 CenterY=6.25 CenterZ=0 NormalX=0 NormalY=0 NormalZ=1 AngleXU=0 Radius=1 StartAngle=2.65709 EndAngle=7.80598
    g13: ArcOfCircle CenterX=0 CenterY=15 CenterZ=0 NormalX=0 NormalY=0 NormalZ=1 AngleXU=0 Radius=9.25 StartAngle=4.58371 EndAngle=4.84107
    g14: ArcOfCircle CenterX=0 CenterY=15 CenterZ=0 NormalX=0 NormalY=0 NormalZ=1 AngleXU=0 Radius=9.25 StartAngle=4.9302 EndAngle=5.17342
    g15: ArcOfCircle CenterX=0 CenterY=15 CenterZ=0 NormalX=0 NormalY=0 NormalZ=1 AngleXU=0 Radius=9.25 StartAngle=5.28965 EndAngle=10.4183
  constraints (51):
    c: PointOnObject(g0,g-2)
    c: Coincident(g1,g0)
    c: Diameter(g0) = 18.5
    c: Diameter(g1) = 22
    c: DistanceY(g-1,g0) = 15
    c: PointOnObject(g2,g-1)
    c: Coincident(g4,g3)
    c: Coincident(g4,g2)
    c: Horizontal(g4)
    c: DistanceX(g2,g-1) = 9
    c: DistanceX(g-1,g3) = 9
    c: DistanceY(g3,g3) = 14
    c: DistanceY(g2,g2) = 14
    c: Horizontal(g5)
    c: Coincident(g6,g5)
    c: Coincident(g7,g5)
    c: DistanceX(g5,g-1) = 5
    c: DistanceX(g-1,g5) = 5
    c: DistanceX(g6,g-1) = 8
    c: DistanceX(g-1,g7) = 8
    c: DistanceY(g-1,g5) = 26
    c: Coincident(g8,g7)
    c: Coincident(g1,g6)
    c: Equal(g1,g8)
    c: Coincident(g1,g8)
    c: Coincident(g8,g3)
    c: Coincident(g1,g2)
    c: Equal(g12,g11)
    c: Equal(g11,g9)
    c: Equal(g9,g10)
    c: Symmetric(g9,g11,g-2)
    c: Symmetric(g10,g12,g-2)
    c: Diameter(g12) = 2
    c: DistanceX(g-1,g11) = 1.75
    c: DistanceY(g-1,g11) = 5
    c: DistanceX(g-1,g12) = 5
    c: DistanceY(g-1,g12) = 6.25
    c: Coincident(g10,g0)
    c: Coincident(g10,g15)
    c: Equal(g0,g13)
    c: Coincident(g0,g13)
    c: Coincident(g9,g13)
    c: Coincident(g9,g0)
    c: Equal(g13,g14)
    c: Coincident(g13,g14)
    c: Coincident(g11,g14)
    c: Coincident(g11,g13)
    c: Equal(g14,g15)
    c: Coincident(g14,g15)
    c: Coincident(g12,g15)
    c: Coincident(g12,g14)
FEATURE [PartDesign::Pad] Pad028
  Direction = (0,-1,-2e-16)
  Length = 180
  Length2 = 10
  Placement = pos=(0,0,0) rot=(1,0,0;1.5708rad)
  Profile = -> Sketch055
  ReferenceAxis = -> Sketch055 [N_Axis]
  Type = 0
FEATURE [PartDesign::Chamfer] Chamfer014
  Angle = 45
  Base = -> Pad028 [Edge12]
  BaseFeature = -> Pad028
  ChamferType = 1
  FlipDirection = false
  Placement = pos=(0,0,0) rot=(1,0,0;1.5708rad)
  Size = 30
  Size2 = 3
  SupportTransform = false
  UseAllEdges = false
FEATURE [PartDesign::Chamfer] Chamfer015
  Angle = 45
  Base = -> Chamfer014 [Edge1,Edge6,Edge9,Edge2]
  BaseFeature = -> Chamfer014
  ChamferType = 0
  FlipDirection = false
  Placement = pos=(0,0,0) rot=(1,0,0;1.5708rad)
  Size = 4
  Size2 = 1
  SupportTransform = false
  UseAllEdges = false
FEATURE [PartDesign::Chamfer] Chamfer016
  Angle = 45
  Base = -> Chamfer015 [Edge8,Edge6,Edge10]
  BaseFeature = -> Chamfer015
  ChamferType = 0
  FlipDirection = false
  Placement = pos=(0,0,0) rot=(1,0,0;1.5708rad)
  Size = 3
  Size2 = 1
  SupportTransform = false
  UseAllEdges = false
FEATURE [PartDesign::Chamfer] Chamfer017
  Angle = 45
  Base = -> Chamfer016 [Edge49,Edge52]
  BaseFeature = -> Chamfer016
  ChamferType = 0
  FlipDirection = false
  Placement = pos=(0,0,0) rot=(1,0,0;1.5708rad)
  Size = 2
  Size2 = 1
  SupportTransform = false
  UseAllEdges = false
FEATURE [Sketcher::SketchObject] Sketch056
  AttachmentOffset = pos=(0,0,20) rot=(0,0,1;0rad)
  FullyConstrained = true
  MapMode = 5
  Placement = pos=(0,-20,-4.4e-15) rot=(1,0,0;1.5708rad)
  Support = -> [XZ_Plane011]
  sketch-geometry (1):
    g0: Circle CenterX=0 CenterY=15 CenterZ=0 NormalX=0 NormalY=0 NormalZ=1 AngleXU=0 Radius=9.25
  constraints (3):
    c: PointOnObject(g0,g-2)
    c: Diameter(g0) = 18.5
    c: DistanceY(g-1,g0) = 15
FEATURE [PartDesign::Pad] Pad029
  BaseFeature = -> Chamfer017
  Direction = (0,-1,-2e-16)
  Length = 3
  Length2 = 10
  Placement = pos=(0,0,0) rot=(1,0,0;1.5708rad)
  Profile = -> Sketch056
  ReferenceAxis = -> Sketch056 [N_Axis]
  Type = 0
FEATURE [Sketcher::SketchObject] Sketch
  ExternalGeometry = -> [Pad029]
  FullyConstrained = true
  MapMode = 5
  Placement = pos=(0,0,0) rot=(1,0,0;1.5708rad)
  Support = -> [XZ_Plane011]
  sketch-geometry (4):
    g0: ArcOfCircle CenterX=0 CenterY=15 CenterZ=0 NormalX=0 NormalY=0 NormalZ=1 AngleXU=0 Radius=9.25 StartAngle=4.54951 EndAngle=4.87527
    g1: LineSegment StartX=-1.5 StartY=5.87243 StartZ=0 EndX=-1.5 EndY=15 EndZ=0
    g2: LineSegment StartX=-1.5 StartY=15 StartZ=0 EndX=1.5 EndY=15 EndZ=0
    g3: LineSegment StartX=1.5 StartY=15 StartZ=0 EndX=1.5 EndY=5.87243 EndZ=0
  constraints (12):
    c: Coincident(g0,g-3)
    c: DistanceX(g0,g0) = 3
    c: PointOnObject(g0,g-5)
    c: Coincident(g1,g0)
    c: Vertical(g1)
    c: Coincident(g2,g1)
    c: Horizontal(g2)
    c: Coincident(g3,g0)
    c: Vertical(g3)
    c: Coincident(g3,g2)
    c: DistanceX(g1,g0) = 1.5
    c: DistanceY(g-1,g1) = 15
FEATURE [PartDesign::LinearPattern] LinearPattern
  BaseFeature = -> Pad029
  Direction = -> Sketch056 [N_Axis]
  Length = 140
  Occurrences = 2
  Originals = -> [Pad029]
  Placement = pos=(0,0,0) rot=(1,0,0;1.5708rad)
FEATURE [PartDesign::Pocket] Pocket022
  BaseFeature = -> LinearPattern
  Direction = (0,1,2e-16)
  Length = 190
  Length2 = 5
  Placement = pos=(0,0,0) rot=(1,0,0;1.5708rad)
  Profile = -> Sketch
  ReferenceAxis = -> Sketch [N_Axis]
  Reversed = true
  Type = 0
FEATURE [Sketcher::SketchObject] Sketch057
  AttachmentOffset = pos=(0,0,23) rot=(0,0,1;0rad)
  ExternalGeometry = -> [Pocket022]
  FullyConstrained = true
  MapMode = 5
  Placement = pos=(0,-23,-5.1e-15) rot=(1,0,0;1.5708rad)
  Support = -> [XZ_Plane011]
  sketch-geometry (8):
    g0: LineSegment StartX=-4.25 StartY=15 StartZ=0 EndX=-3.25 EndY=15 EndZ=0
    g1: LineSegment StartX=-3.25 StartY=15 StartZ=0 EndX=-3.25 EndY=6.68601 EndZ=0
    g2: LineSegment StartX=-4.25 StartY=7.15 StartZ=0 EndX=-4.25 EndY=15 EndZ=0
    g3: LineSegment StartX=3.25 StartY=15 StartZ=0 EndX=4.25 EndY=15 EndZ=0
    g4: LineSegment StartX=4.25 StartY=15 StartZ=0 EndX=4.25 EndY=7.15 EndZ=0
    g5: LineSegment StartX=3.25 StartY=6.68601 StartZ=0 EndX=3.25 EndY=15 EndZ=0
    g6: ArcOfCircle CenterX=0 CenterY=15 CenterZ=0 NormalX=0 NormalY=0 NormalZ=1 AngleXU=0 Radius=8.92665 StartAngle=4.21617 EndAngle=4.33975
    g7: ArcOfCircle CenterX=0 CenterY=15 CenterZ=0 NormalX=0 NormalY=0 NormalZ=1 AngleXU=0 Radius=8.92665 StartAngle=5.08503 EndAngle=5.20861
  constraints (24):
    c: Coincident(g0,g1)
    c: Coincident(g2,g0)
    c: Horizontal(g0)
    c: Vertical(g1)
    c: Vertical(g2)
    c: Coincident(g3,g4)
    c: Coincident(g5,g3)
    c: Horizontal(g3)
    c: Vertical(g4)
    c: Vertical(g5)
    c: DistanceX(g0,g3) = 6.5
    c: DistanceX(g0,g0) = 1
    c: DistanceX(g3,g3) = 1
    c: DistanceX(g0,g-3) = 3.25
    c: DistanceY(g-1,g0) = 15
    c: DistanceY(g-1,g3) = 15
    c: Coincident(g6,g-3)
    c: Coincident(g6,g2)
    c: Coincident(g6,g1)
    c: Coincident(g7,g6)
    c: Coincident(g7,g5)
    c: Coincident(g7,g4)
    c: DistanceY(g4,g4) = 7.85
    c: DistanceY(g2,g2) = 7.85
FEATURE [PartDesign::Pad] Pad
  BaseFeature = -> Pocket022
  Direction = (0,-1,-2e-16)
  Length = 1
  Length2 = 10
  Placement = pos=(0,0,0) rot=(1,0,0;1.5708rad)
  Profile = -> Sketch057
  ReferenceAxis = -> Sketch057 [N_Axis]
  Type = 0
FEATURE [Sketcher::SketchObject] Sketch058
  AttachmentOffset = pos=(0,0,24) rot=(0,0,1;0rad)
  ExternalGeometry = -> [Pad]
  FullyConstrained = true
  MapMode = 5
  Placement = pos=(0,-24,-5.3e-15) rot=(1,0,0;1.5708rad)
  Support = -> [XZ_Plane011]
  sketch-geometry (8):
    g0: LineSegment StartX=-4.25 StartY=15 StartZ=0 EndX=-2.25 EndY=15 EndZ=0
    g1: LineSegment StartX=-2.25 StartY=15 StartZ=0 EndX=-2.25 EndY=6.3 EndZ=0
    g2: LineSegment StartX=-4.25 StartY=7.0823 StartZ=0 EndX=-4.25 EndY=15 EndZ=0
    g3: LineSegment StartX=4.25 StartY=15 StartZ=0 EndX=2.25 EndY=15 EndZ=0
    g4: LineSegment StartX=2.25 StartY=15 StartZ=0 EndX=2.25 EndY=6.3 EndZ=0
    g5: LineSegment StartX=4.25 StartY=7.0823 StartZ=0 EndX=4.25 EndY=15 EndZ=0
    g6: ArcOfCircle CenterX=0 CenterY=15 CenterZ=0 NormalX=0 NormalY=0 NormalZ=1 AngleXU=0 Radius=8.98624 StartAngle=4.21976 EndAngle=4.45931
    g7: ArcOfCircle CenterX=0 CenterY=15 CenterZ=0 NormalX=0 NormalY=0 NormalZ=1 AngleXU=0 Radius=8.98624 StartAngle=4.96546 EndAngle=5.20502
  constraints (22):
    c: Coincident(g0,g1)
    c: Coincident(g2,g0)
    c: Horizontal(g0)
    c: Vertical(g1)
    c: Vertical(g2)
    c: Coincident(g0,g-3)
    c: Coincident(g3,g4)
    c: Coincident(g5,g3)
    c: Horizontal(g3)
    c: Vertical(g4)
    c: Vertical(g5)
    c: Coincident(g3,g-4)
    c: DistanceX(g3,g3) = 2
    c: DistanceX(g0,g0) = 2
    c: Coincident(g6,g-5)
    c: Coincident(g6,g2)
    c: Coincident(g6,g1)
    c: Coincident(g7,g6)
    c: Coincident(g7,g4)
    c: Coincident(g7,g5)
    c: DistanceY(g1,g1) = 8.7
    c: DistanceY(g4,g4) = 8.7
FEATURE [PartDesign::Pad] Pad030
  BaseFeature = -> Pad
  Direction = (0,-1,-2e-16)
  Length = 1
  Length2 = 10
  Placement = pos=(0,0,0) rot=(1,0,0;1.5708rad)
  Profile = -> Sketch058
  ReferenceAxis = -> Sketch058 [N_Axis]
  Type = 0
FEATURE [Sketcher::SketchObject] Sketch059
  AttachmentOffset = pos=(0,0,160) rot=(0,0,1;0rad)
  ExternalGeometry = -> [Pad030]
  FullyConstrained = true
  MapMode = 5
  Placement = pos=(0,-160,-3.55e-14) rot=(1,0,0;1.5708rad)
  Support = -> [XZ_Plane011]
  sketch-geometry (8):
    g0: LineSegment StartX=-4.25 StartY=15 StartZ=0 EndX=-3.25 EndY=15 EndZ=0
    g1: LineSegment StartX=-3.25 StartY=15 StartZ=0 EndX=-3.25 EndY=6.68601 EndZ=0
    g2: LineSegment StartX=-3.25 StartY=6.68601 StartZ=0 EndX=-4.25 EndY=6.68601 EndZ=0
    g3: LineSegment StartX=-4.25 StartY=6.68601 StartZ=0 EndX=-4.25 EndY=15 EndZ=0
    g4: LineSegment StartX=3.25 StartY=15 StartZ=0 EndX=4.25 EndY=15 EndZ=0
    g5: LineSegment StartX=4.25 StartY=15 StartZ=0 EndX=4.25 EndY=6.68601 EndZ=0
    g6: LineSegment StartX=4.25 StartY=6.68601 StartZ=0 EndX=3.25 EndY=6.68601 EndZ=0
    g7: LineSegment StartX=3.25 StartY=6.68601 StartZ=0 EndX=3.25 EndY=15 EndZ=0
  constraints (19):
    c: Coincident(g0,g1)
    c: Coincident(g1,g2)
    c: Coincident(g2,g3)
    c: Coincident(g3,g0)
    c: Horizontal(g0)
    c: Horizontal(g2)
    c: Vertical(g1)
    c: Vertical(g3)
    c: Coincident(g0,g-8)
    c: Coincident(g1,g-3)
    c: Coincident(g4,g5)
    c: Coincident(g5,g6)
    c: Coincident(g6,g7)
    c: Coincident(g7,g4)
    c: Horizontal(g6)
    c: Vertical(g5)
    c: Coincident(g4,g-5)
    c: Coincident(g6,g-5)
    c: Coincident(g4,g-7)
FEATURE [PartDesign::Pad] Pad031
  BaseFeature = -> Pad030
  Direction = (0,-1,-2e-16)
  Length = 1
  Length2 = 10
  Placement = pos=(0,0,0) rot=(1,0,0;1.5708rad)
  Profile = -> Sketch059
  ReferenceAxis = -> Sketch059 [N_Axis]
  Reversed = true
  Type = 0
FEATURE [Sketcher::SketchObject] Sketch060
  AttachmentOffset = pos=(0,0,159) rot=(0,0,1;0rad)
  ExternalGeometry = -> [Pad031]
  FullyConstrained = true
  MapMode = 5
  Placement = pos=(0,-159,-3.53e-14) rot=(1,0,0;1.5708rad)
  Support = -> [XZ_Plane011]
  sketch-geometry (8):
    g0: LineSegment StartX=-4.25 StartY=15 StartZ=0 EndX=-2.25 EndY=15 EndZ=0
    g1: LineSegment StartX=-2.25 StartY=15 StartZ=0 EndX=-2.25 EndY=6.68601 EndZ=0
    g2: LineSegment StartX=-2.25 StartY=6.68601 StartZ=0 EndX=-4.25 EndY=6.68601 EndZ=0
    g3: LineSegment StartX=-4.25 StartY=6.68601 StartZ=0 EndX=-4.25 EndY=15 EndZ=0
    g4: LineSegment StartX=2.25 StartY=15 StartZ=0 EndX=4.25 EndY=15 EndZ=0
    g5: LineSegment StartX=4.25 StartY=15 StartZ=0 EndX=4.25 EndY=6.68601 EndZ=0
    g6: LineSegment StartX=4.25 StartY=6.68601 StartZ=0 EndX=2.25 EndY=6.68601 EndZ=0
    g7: LineSegment StartX=2.25 StartY=6.68601 StartZ=0 EndX=2.25 EndY=15 EndZ=0
  constraints (18):
    c: Coincident(g0,g1)
    c: Coincident(g1,g2)
    c: Coincident(g2,g3)
    c: Coincident(g3,g0)
    c: Horizontal(g2)
    c: Vertical(g1)
    c: Coincident(g0,g-3)
    c: Coincident(g4,g5)
    c: Coincident(g5,g6)
    c: Coincident(g6,g7)
    c: Coincident(g7,g4)
    c: Horizontal(g6)
    c: Vertical(g7)
    c: Coincident(g4,g-4)
    c: Coincident(g4,g-4)
    c: Coincident(g0,g-3)
    c: Coincident(g2,g-6)
    c: Coincident(g-9,g5)
FEATURE [PartDesign::Pad] Pad032
  BaseFeature = -> Pad031
  Direction = (0,-1,-2e-16)
  Length = 1
  Length2 = 10
  Placement = pos=(0,0,0) rot=(1,0,0;1.5708rad)
  Profile = -> Sketch060
  ReferenceAxis = -> Sketch060 [N_Axis]
  Reversed = true
  Type = 0
FEATURE [Sketcher::SketchObject] Sketch061
  AttachmentOffset = pos=(0,0,5) rot=(0,0,1;0rad)
  FullyConstrained = true
  MapMode = 5
  Placement = pos=(0,0,5) rot=(0,0,1;0rad)
  Support = -> [XY_Plane011]
  sketch-geometry (4):
    g0: Circle CenterX=-7 CenterY=-16 CenterZ=0 NormalX=0 NormalY=0 NormalZ=1 AngleXU=0 Radius=3
    g1: Circle CenterX=7 CenterY=-16 CenterZ=0 NormalX=0 NormalY=0 NormalZ=1 AngleXU=0 Radius=3
    g2: Circle CenterX=-7 CenterY=-170 CenterZ=0 NormalX=0 NormalY=0 NormalZ=1 AngleXU=0 Radius=3
    g3: Circle CenterX=7 CenterY=-170 CenterZ=0 NormalX=0 NormalY=0 NormalZ=1 AngleXU=0 Radius=3
  constraints (10):
    c: Symmetric(g1,g0,g-2)
    c: Equal(g1,g0)
    c: Diameter(g1) = 6
    c: DistanceY(g1,g-1) = 16
    c: DistanceX(g-1,g1) = 7
    c: Symmetric(g3,g2,g-2)
    c: Equal(g3,g2)
    c: Diameter(g3) = 6
    c: DistanceX(g-1,g3) = 7
    c: DistanceY(g3,g-1) = 170
FEATURE [PartDesign::Pad] Pad033
  BaseFeature = -> Pad032
  Direction = (0,0,1)
  Length = 23
  Length2 = 10
  Placement = pos=(0,0,0) rot=(1,0,0;1.5708rad)
  Profile = -> Sketch061
  ReferenceAxis = -> Sketch061 [N_Axis]
  Type = 0
FEATURE [Sketcher::SketchObject] Sketch062
  ExternalGeometry = -> [Pad033]
  FullyConstrained = false
  MapMode = 5
  Placement = pos=(0,0,0) rot=(1,0,0;1.5708rad)
  Support = -> [XZ_Plane011]
  sketch-geometry (12):
    g0: ArcOfCircle CenterX=0 CenterY=15 CenterZ=0 NormalX=0 NormalY=0 NormalZ=1 AngleXU=0 Radius=11 StartAngle=0.421458 EndAngle=2.72014
    g1: LineSegment StartX=-18.5389 StartY=30.1793 StartZ=0 EndX=17.9106 EndY=30.1793 EndZ=0
    g2: LineSegment StartX=17.9106 StartY=30.1793 StartZ=0 EndX=17.9106 EndY=19.5 EndZ=0
    g3: LineSegment StartX=17.9106 StartY=19.5 StartZ=0 EndX=10.0374 EndY=19.5 EndZ=0
    g4: LineSegment StartX=-18.5389 StartY=19.5 StartZ=0 EndX=-18.5389 EndY=30.1793 EndZ=0
    g5: LineSegment StartX=-10.0374 StartY=19.5 StartZ=0 EndX=-18.5389 EndY=19.5 EndZ=0
    g6: LineSegment StartX=-10.185 StartY=8.48803 StartZ=0 EndX=-9.55305 EndY=3.96158 EndZ=0
    g7: LineSegment StartX=-9.55305 StartY=3.96158 StartZ=0 EndX=-10.185 EndY=3.96158 EndZ=0
    g8: LineSegment StartX=-10.185 StartY=3.96158 StartZ=0 EndX=-10.185 EndY=8.48803 EndZ=0
    g9: LineSegment StartX=9.55305 StartY=3.96158 StartZ=0 EndX=10.185 EndY=8.48803 EndZ=0
    g10: LineSegment StartX=10.185 StartY=8.48803 StartZ=0 EndX=10.185 EndY=3.96158 EndZ=0
    g11: LineSegment StartX=10.185 StartY=3.96158 StartZ=0 EndX=9.55305 EndY=3.96158 EndZ=0
  constraints (28):
    c: Coincident(g0,g-3)
    c: Coincident(g1,g2)
    c: Coincident(g2,g3)
    c: Coincident(g5,g4)
    c: Coincident(g4,g1)
    c: Horizontal(g1)
    c: Horizontal(g3)
    c: Vertical(g2)
    c: Vertical(g4)
    c: PointOnObject(g0,g3)
    c: Diameter(g0) = 22
    c: DistanceY(g-1,g2) = 19.5
    c: Coincident(g3,g0)
    c: PointOnObject(g5,g0)
    c: Coincident(g6,g-4)
    c: Coincident(g6,g-4)
    c: Coincident(g7,g6)
    c: Coincident(g8,g7)
    c: Coincident(g8,g6)
    c: Vertical(g8)
    c: Coincident(g9,g-5)
    c: Coincident(g9,g-5)
    c: Coincident(g10,g9)
    c: Vertical(g10)
    c: Coincident(g11,g10)
    c: Coincident(g11,g9)
    c: Horizontal(g7)
    c: Horizontal(g11)
FEATURE [PartDesign::Pocket] Pocket023
  BaseFeature = -> Pad033
  Direction = (0,1,2e-16)
  Length = 183
  Length2 = 5
  Placement = pos=(0,0,0) rot=(1,0,0;1.5708rad)
  Profile = -> Sketch062
  ReferenceAxis = -> Sketch062 [N_Axis]
  Reversed = true
  Type = 0
FEATURE [Sketcher::SketchObject] Sketch063
  AttachmentOffset = pos=(0,0,8) rot=(0,0,1;0rad)
  FullyConstrained = true
  MapMode = 5
  Placement = pos=(0,0,8) rot=(0,0,1;0rad)
  Support = -> [XY_Plane011]
  sketch-geometry (4):
    g0: Circle CenterX=7 CenterY=-170 CenterZ=0 NormalX=0 NormalY=0 NormalZ=1 AngleXU=0 Radius=2
    g1: Circle CenterX=-7 CenterY=-170 CenterZ=0 NormalX=0 NormalY=0 NormalZ=1 AngleXU=0 Radius=2
    g2: Circle CenterX=7 CenterY=-16 CenterZ=0 NormalX=0 NormalY=0 NormalZ=1 AngleXU=0 Radius=2
    g3: Circle CenterX=-7 CenterY=-16 CenterZ=0 NormalX=0 NormalY=0 NormalZ=1 AngleXU=0 Radius=2
  constraints (10):
    c: Symmetric(g2,g3,g-2)
    c: Symmetric(g1,g0,g-2)
    c: Equal(g2,g3)
    c: Equal(g2,g0)
    c: Equal(g2,g1)
    c: Diameter(g2) = 4
    c: DistanceY(g0,g-1) = 170
    c: DistanceX(g-1,g0) = 7
    c: DistanceX(g-1,g2) = 7
    c: DistanceY(g2,g-1) = 16
FEATURE [PartDesign::Pocket] Pocket024
  BaseFeature = -> Pocket023
  Direction = (0,0,-1)
  Length = 21
  Length2 = 5
  Placement = pos=(0,0,0) rot=(1,0,0;1.5708rad)
  Profile = -> Sketch063
  ReferenceAxis = -> Sketch063 [N_Axis]
  Reversed = true
  Type = 0
FEATURE [PartDesign::Chamfer] Chamfer018
  Angle = 45
  Base = -> Pocket024 [Edge57,Edge54,Edge56,Edge53]
  BaseFeature = -> Pocket024
  ChamferType = 0
  FlipDirection = false
  Placement = pos=(0,0,0) rot=(1,0,0;1.5708rad)
  Size = 1.5
  Size2 = 1
  SupportTransform = false
  UseAllEdges = false
FEATURE [Sketcher::SketchObject] Sketch064
  AttachmentOffset = pos=(0,0,4) rot=(0,0,1;0rad)
  FullyConstrained = true
  MapMode = 5
  Placement = pos=(0,0,4) rot=(0,0,1;0rad)
  Support = -> [XY_Plane011]
  sketch-geometry (1):
    g0: Circle CenterX=0 CenterY=-9 CenterZ=0 NormalX=0 NormalY=0 NormalZ=1 AngleXU=0 Radius=2.5
  constraints (3):
    c: Diameter(g0) = 5
    c: DistanceY(g0,g-1) = 9
    c: PointOnObject(g0,g-2)
FEATURE [PartDesign::Pad] Pad034
  BaseFeature = -> Chamfer018
  Direction = (0,0,1)
  Length = 21
  Length2 = 10
  Placement = pos=(0,0,0) rot=(1,0,0;1.5708rad)
  Profile = -> Sketch064
  ReferenceAxis = -> Sketch064 [N_Axis]
  Type = 0
FEATURE [Sketcher::SketchObject] Sketch065
  AttachmentOffset = pos=(0,0,5) rot=(0,0,1;0rad)
  FullyConstrained = true
  MapMode = 5
  Placement = pos=(0,-5,-1.1e-15) rot=(1,0,0;1.5708rad)
  Support = -> [XZ_Plane011]
  sketch-geometry (1):
    g0: Circle CenterX=0 CenterY=15 CenterZ=0 NormalX=0 NormalY=0 NormalZ=1 AngleXU=0 Radius=9
  constraints (3):
    c: PointOnObject(g0,g-2)
    c: Diameter(g0) = 18
    c: DistanceY(g-1,g0) = 15
FEATURE [PartDesign::Pocket] Pocket025
  BaseFeature = -> Pad034
  Direction = (0,1,2e-16)
  Length = 7
  Length2 = 5
  Placement = pos=(0,0,0) rot=(1,0,0;1.5708rad)
  Profile = -> Sketch065
  ReferenceAxis = -> Sketch065 [N_Axis]
  Reversed = true
  Type = 0
FEATURE [PartDesign::Body] Body011  label="Shell"
  Group = -> [Sketch055,Pad028,Chamfer014,Chamfer015,Chamfer016,Chamfer017,Sketch056,Pad029,Sketch,LinearPattern,Pocket022,Sketch057,Pad,Sketch058,Pad030,Sketch059,Pad031,Sketch060,Pad032,Sketch061,Pad033,Sketch062,Pocket023,Sketch063,Pocket024,Chamfer018,Sketch064,Pad034,Sketch065,Pocket025]
  Origin = -> Origin011
  Tip = -> Pocket025
